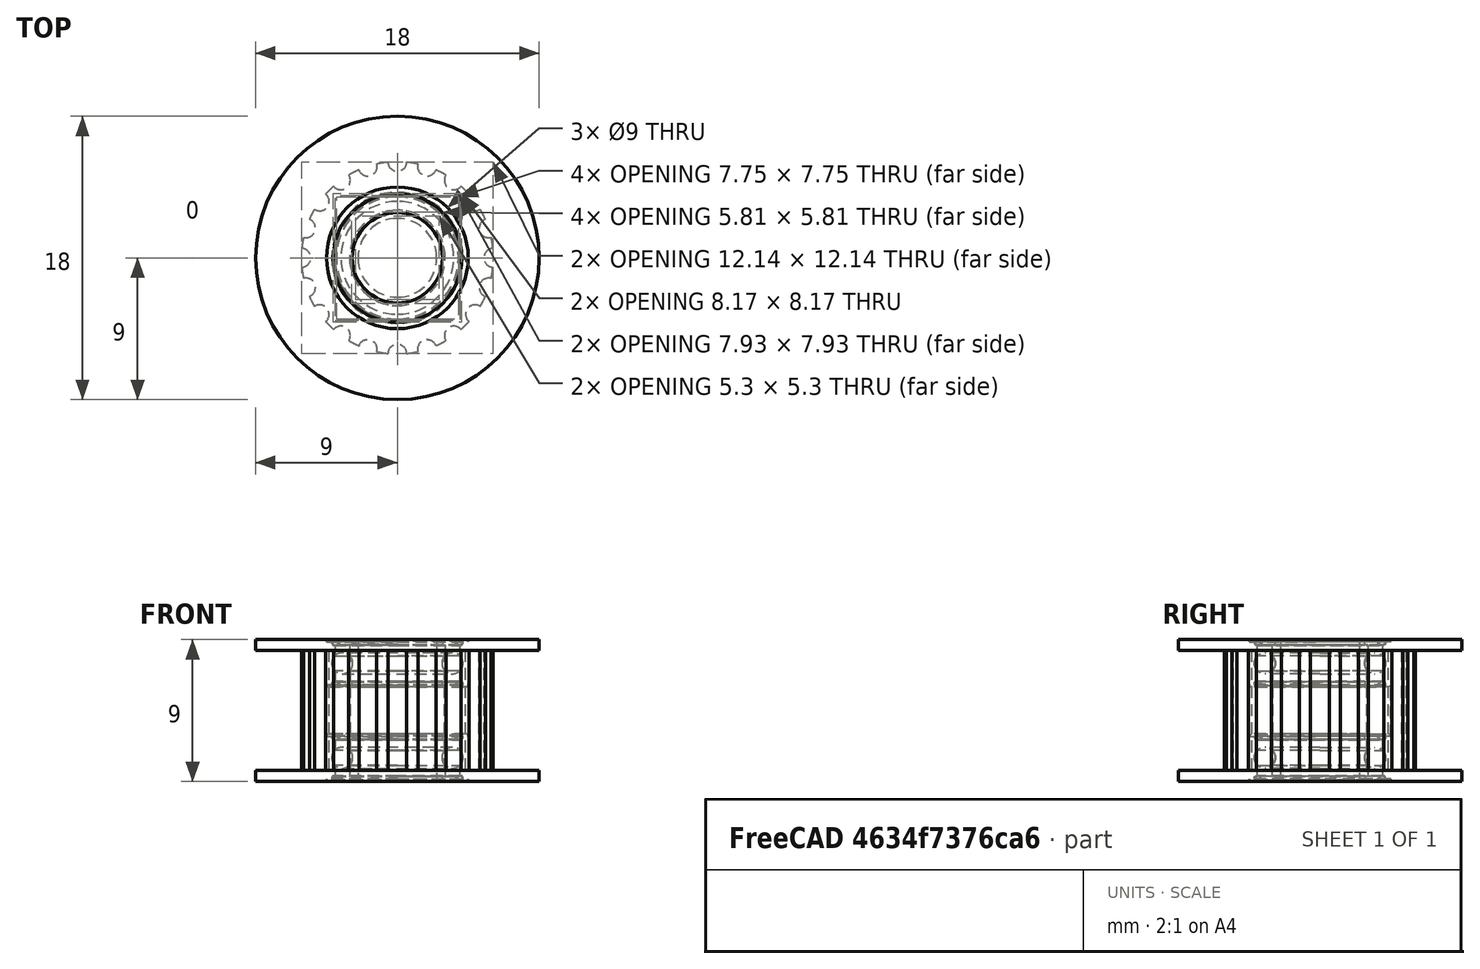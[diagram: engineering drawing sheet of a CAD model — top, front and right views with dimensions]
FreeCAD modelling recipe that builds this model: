
FCSTD DOCUMENT  (FreeCAD 0.16R4945 (Git))
Label: GT2Bearing
License: CC-BY 3.0
LicenseURL: http://creativecommons.org/licenses/by/3.0/
objects: Part::FeaturePython×3, Sketcher::SketchObject×3, Part::Cylinder×2, PartDesign::Pad×2, Part::Cut×1, PartDesign::Pocket×1, Part::MultiFuse×1
note: 16 computed .brp shape members not serialized (recipe doc carries the construction recipe); baked Part::Feature solids carry a one-line shape summary decoded from their .brp

FEATURE [Part::Cylinder] Cylinder  label="Cilindro"
  Angle = 360
  Height = 7.6
  Placement = pos=(6.1,0,0) rot=(0,0,1;0rad)
  Radius = 0.6
FEATURE [Part::FeaturePython] Array  # Draft array (typed FeaturePython)
  Angle = 360
  ArrayType = 1
  Axis = (0,0,1)
  Base = -> Cylinder
  Center = (0,0,0)
  IntervalX = (1,0,0)
  IntervalY = (0,1,0)
  IntervalZ = (0,0,1)
  NumberPolar = 20
  NumberX = 2
  NumberY = 2
  NumberZ = 1
FEATURE [Part::Cylinder] Cylinder001  label="Cilindro001"
  Angle = 360
  Height = 7.6
  Radius = 6.1
FEATURE [Part::Cut] Cut
  Base = -> Cylinder001
  Placement = pos=(0,0,1) rot=(0,0,1;0rad)
  Tool = -> Array
FEATURE [Sketcher::SketchObject] Sketch
  Placement = pos=(0,0,8.6) rot=(0,0,1;0rad)
  Support = -> Cut [Face2]
  sketch-geometry (1):
    g0: Circle CenterX=0 CenterY=0 CenterZ=0 NormalX=0 NormalY=0 NormalZ=1 Radius=9
  constraints (2):
    c: Coincident(g0,g-1)
    c: Radius(g0) = 9
FEATURE [PartDesign::Pad] Pad
  Length = 0.7
  Length2 = 100
  Placement = pos=(0,0,1) rot=(0,0,1;0rad)
  Sketch = -> Sketch
  Type = 0
FEATURE [Sketcher::SketchObject] Sketch001
  Placement = pos=(0,0,1) rot=(1,0,0;3.14159rad)
  Support = -> Pad [Face44]
  sketch-geometry (1):
    g0: Circle CenterX=0 CenterY=0 CenterZ=0 NormalX=0 NormalY=0 NormalZ=1 Radius=9
  constraints (2):
    c: Coincident(g0,g-1)
    c: Radius(g0) = 9
FEATURE [PartDesign::Pad] Pad001
  Length = 0.7
  Length2 = 100
  Placement = pos=(0,0,1) rot=(0,0,1;0rad)
  Sketch = -> Sketch001
  Type = 0
FEATURE [Sketcher::SketchObject] Sketch002
  Placement = pos=(0,0,9.3) rot=(0,0,1;0rad)
  Support = -> Pad001 [Face3]
  sketch-geometry (1):
    g0: Circle CenterX=0 CenterY=0 CenterZ=0 NormalX=0 NormalY=0 NormalZ=1 Radius=4.5
  constraints (2):
    c: Coincident(g0,g-1)
    c: Radius(g0) = 4.5
FEATURE [PartDesign::Pocket] Pocket
  Length = 5
  Placement = pos=(0,0,1) rot=(0,0,1;0rad)
  Sketch = -> Sketch002
  Type = 1
FEATURE [Part::FeaturePython] bearing_mr95zz_2_stp1_01  # a2plus imported part (geometry in sourceFile) (typed FeaturePython)
  Placement = pos=(0,0,3.3) rot=(0,1,0;1.5708rad)
  fixedPosition = true
  sourceFile = <userpath>/Downloads/bearing_mr95zz_2/bearing_mr95zz_2.stp
  timeLastImport = 1444938472
  updateColors = true
FEATURE [Part::FeaturePython] bearing_mr95zz_2_stp1_002  # a2plus imported part (geometry in sourceFile) (typed FeaturePython)
  Placement = pos=(0,0,9.3) rot=(0,1,0;1.5708rad)
  fixedPosition = true
  sourceFile = <userpath>/Downloads/bearing_mr95zz_2/bearing_mr95zz_2.stp
  timeLastImport = 1444938472
  updateColors = true
FEATURE [Part::MultiFuse] Fusion
  Shapes = -> [Pocket,bearing_mr95zz_2_stp1_01,bearing_mr95zz_2_stp1_002]
